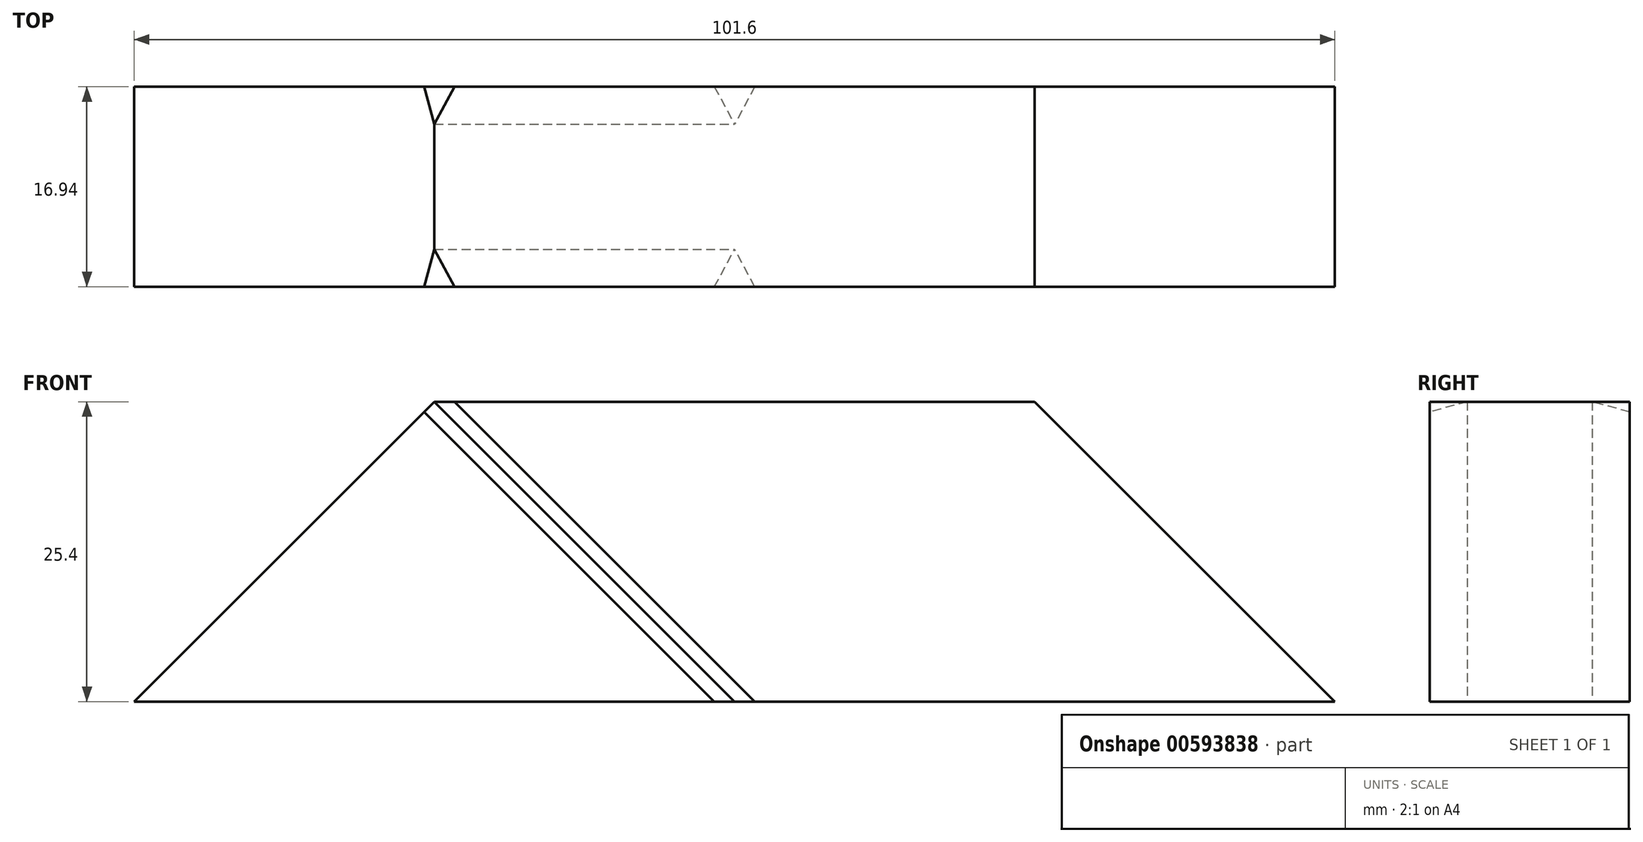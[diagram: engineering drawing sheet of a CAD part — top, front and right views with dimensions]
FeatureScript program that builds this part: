
annotation { "Feature Type Name" : "Feature", "Feature Type Description" : "" }
export const myFeature = defineFeature(function(context is Context, id is Id, definition is map)
    precondition{}
    {
        {
            var Q0;
            Q0=qCreatedBy(makeId("Front.planeOp"),FACE);
            var sketch = newSketch(context, id + "F0", { "sketchPlane" : qUnion([Q0])});
            skLineSegment(sketch, "E0.bottom", {"start": v(-50.8, 12.7) * mm, "end": v(50.8, 12.7) * mm});
            skLineSegment(sketch, "E0.top", {"start": v(-50.8, -12.7) * mm, "end": v(50.8, -12.7) * mm});
            skLineSegment(sketch, "E0.left", {"start": v(-50.8, 12.7) * mm, "end": v(-50.8, -12.7) * mm});
            skLineSegment(sketch, "E0.right", {"start": v(50.8, 12.7) * mm, "end": v(50.8, -12.7) * mm});
            skPoint(sketch, "E0.middle", {"position": v(0, 0) * mm});
            skSolve(sketch);
        }
        {
            var Q0;
            Q0=makeQuery(id+"F0.imprint","IMPRINT",FACE,{"disambiguationData":[TD([[makeQuery(id+"F0.imprint","IMPRINT",EDGE,{"derivedFrom":sQuery(id+"F0.wireOp",EDGE,"E0.bottom")}),-1.0]])]});
            extrude(context, id + "F1", {"entities" : qUnion([Q0]), "endBound" : BoundingType.SYMMETRIC, "depth" : 16.93 * mm, "offsetDistance" : 25.4 * mm});
        }
        {
            var Q0;
            Q0=makeQuery(id+"F1.opExtrude","SWEPT_EDGE",EDGE,{"disambiguationData":[OSD([sQuery(id+"F0.wireOp",EDGE,"E0.bottom"),sQuery(id+"F0.wireOp",EDGE,"E0.left")])]});
            var Q1;
            Q1=makeQuery(id+"F1.opExtrude","SWEPT_EDGE",EDGE,{"disambiguationData":[OSD([sQuery(id+"F0.wireOp",EDGE,"E0.bottom"),sQuery(id+"F0.wireOp",EDGE,"E0.right")])]});
            chamfer(context, id + "F2", {"entities" : qUnion([Q0, Q1]), "width" : 25.4 * mm, "tangentPropagation" : true});
        }
        {
            var Q0;
            Q0=makeQuery(id+"F1.opExtrude","SWEPT_FACE",FACE,{"disambiguationData":[OSD([sQuery(id+"F0.wireOp",EDGE,"E0.bottom")])]});
            var sketch = newSketch(context, id + "F3", { "sketchPlane" : qUnion([Q0])});
            skSolve(sketch);
        }
        {
            var Q0;
            {var subQ0=sQuery(id+"F0.wireOp",EDGE,"E0.bottom");Q0=makeQuery(id+"F3.imprint","IMPRINT",FACE,{"disambiguationData":[TD([[makeQuery(id+"F3.imprint","IMPRINT",EDGE,{"derivedFrom":makeQuery(id+"F1.opExtrude","CAP_EDGE",EDGE,{"disambiguationData":[OSD([subQ0])],"isStart":true})}),-1.0]])]});}
            var sketch = newSketch(context, id + "F4", { "sketchPlane" : qUnion([Q0])});
            skLineSegment(sketch, "E1", {"start": v(-25.4, -8.47) * mm, "end": v(-23.69, -8.47) * mm});
            skLineSegment(sketch, "E2", {"start": v(-23.69, -8.47) * mm, "end": v(-25.4, -5.3) * mm});
            skLineSegment(sketch, "E3.MirrorCS", {"start": v(-27.11, -8.47) * mm, "end": v(-25.4, -5.3) * mm});
            skLineSegment(sketch, "E4", {"start": v(-27.11, -8.47) * mm, "end": v(-23.69, -8.47) * mm});
            skLineSegment(sketch, "E5.MirrorCS", {"start": v(-25.4, 8.47) * mm, "end": v(-23.69, 8.47) * mm});
            skLineSegment(sketch, "E6.MirrorCS", {"start": v(-27.11, 8.47) * mm, "end": v(-23.69, 8.47) * mm});
            skLineSegment(sketch, "E7.MirrorCS", {"start": v(-27.11, 8.47) * mm, "end": v(-25.4, 5.3) * mm});
            skLineSegment(sketch, "E8.MirrorCS", {"start": v(-23.69, 8.47) * mm, "end": v(-25.4, 5.3) * mm});
            skSolve(sketch);
        }
        {
            var Q0;
            Q0=makeQuery(id+"F1.opExtrude","CAP_FACE",FACE,{"disambiguationData":[OSD([sQuery(id+"F0.wireOp",EDGE,"E0.bottom"),sQuery(id+"F0.wireOp",EDGE,"E0.top"),sQuery(id+"F0.wireOp",EDGE,"E0.left"),sQuery(id+"F0.wireOp",EDGE,"E0.right")])],"isStart":false});
            var sketch = newSketch(context, id + "F5", { "sketchPlane" : qUnion([Q0])});
            skLineSegment(sketch, "E9", {"start": v(-25.4, 12.7) * mm, "end": v(-25.4, -12.7) * mm, "construction": true});
            skLineSegment(sketch, "E10", {"start": v(-25.4, -12.7) * mm, "end": v(-50.8, -12.7) * mm, "construction": true});
            skLineSegment(sketch, "E11", {"start": v(-25.4, -12.7) * mm, "end": v(0, -12.7) * mm, "construction": true});
            skLineSegment(sketch, "E12", {"start": v(0, -12.7) * mm, "end": v(-25.4, 12.7) * mm});
            skSolve(sketch);
        }
        {
            var Q0;
            {var subQ0=sQuery(id+"F5.wireOp",EDGE,"E12");Q0=makeQuery(id+"F5.imprint","IMPRINT",FACE,{"disambiguationData":[TD([[makeQuery(id+"F5.imprint","IMPRINT",EDGE,{"derivedFrom":subQ0}),-1.0]])]});}
            var sketch = newSketch(context, id + "F6", { "sketchPlane" : qUnion([Q0])});
            skLineSegment(sketch, "E13.0.0", {"start": v(-25.4, 12.7) * mm, "end": v(0, -12.7) * mm, "construction": true});
            skLineSegment(sketch, "E13.0.1", {"start": v(0, -12.7) * mm, "end": v(50.8, -12.7) * mm, "construction": true});
            skLineSegment(sketch, "E13.0.2", {"start": v(50.8, -12.7) * mm, "end": v(25.4, 12.7) * mm, "construction": true});
            skLineSegment(sketch, "E13.0.3", {"start": v(25.4, 12.7) * mm, "end": v(-25.4, 12.7) * mm, "construction": true});
            skLineSegment(sketch, "E13.1.0", {"start": v(-50.8, -12.7) * mm, "end": v(0, -12.7) * mm});
            skLineSegment(sketch, "E13.1.1", {"start": v(0, -12.7) * mm, "end": v(-25.4, 12.7) * mm});
            skLineSegment(sketch, "E13.1.2", {"start": v(-25.4, 12.7) * mm, "end": v(-50.8, -12.7) * mm, "construction": true});
            skLineSegment(sketch, "E14", {"start": v(50.8, -12.7) * mm, "end": v(25.4, -12.7) * mm, "construction": true});
            skLineSegment(sketch, "E15", {"start": v(25.4, -12.7) * mm, "end": v(0, -12.7) * mm, "construction": true});
            skLineSegment(sketch, "E16", {"start": v(0, -12.7) * mm, "end": v(25.4, 12.7) * mm});
            skSolve(sketch);
        }
        {
            var Q0;
            {var subQ0=sQuery(id+"F4.wireOp",EDGE,"E3.MirrorCS");Q0=makeQuery(id+"F4.imprint","IMPRINT",FACE,{"disambiguationData":[TD([[makeQuery(id+"F4.imprint","IMPRINT",EDGE,{"derivedFrom":subQ0}),-1.0]])]});}
            var Q1;
            {var subQ4=sQuery(id+"F4.wireOp",EDGE,"E7.MirrorCS");Q1=makeQuery(id+"F4.imprint","IMPRINT",FACE,{"disambiguationData":[TD([[makeQuery(id+"F4.imprint","IMPRINT",EDGE,{"derivedFrom":subQ4}),1.0]])]});}
            var Q2;
            {var subQ0=sQuery(id+"F4.wireOp",EDGE,"E2");Q2=makeQuery(id+"F4.imprint","IMPRINT",FACE,{"disambiguationData":[TD([[makeQuery(id+"F4.imprint","IMPRINT",EDGE,{"derivedFrom":subQ0}),1.0]])]});}
            var Q3;
            {var subQ4=sQuery(id+"F4.wireOp",EDGE,"E8.MirrorCS");Q3=makeQuery(id+"F4.imprint","IMPRINT",FACE,{"disambiguationData":[TD([[makeQuery(id+"F4.imprint","IMPRINT",EDGE,{"derivedFrom":subQ4}),-1.0]])]});}
            var Q4;
            {var subQ4=sQuery(id+"F4.wireOp",EDGE,"dd271e9e-a8f9-4583-93ba-da34ee3789db0.MirrorCS");Q4=makeQuery(id+"F4.imprint","IMPRINT",FACE,{"disambiguationData":[TD([[makeQuery(id+"F4.imprint","IMPRINT",EDGE,{"derivedFrom":subQ4}),-1.0]])]});}
            var Q5;
            {var subQ4=sQuery(id+"F4.wireOp",EDGE,"3a3def27-543b-4b22-b4b6-f03de71b3d630.MirrorCS");Q5=makeQuery(id+"F4.imprint","IMPRINT",FACE,{"disambiguationData":[TD([[makeQuery(id+"F4.imprint","IMPRINT",EDGE,{"derivedFrom":subQ4}),1.0]])]});}
            var Q6;
            {var subQ0=sQuery(id+"F4.wireOp",EDGE,"d168a0cd-3c3a-453f-922a-891af3fde8110.MirrorCS");Q6=makeQuery(id+"F4.imprint","IMPRINT",FACE,{"disambiguationData":[TD([[makeQuery(id+"F4.imprint","IMPRINT",EDGE,{"derivedFrom":subQ0}),-1.0]])]});}
            var Q7;
            {var subQ0=sQuery(id+"F4.wireOp",EDGE,"236fdeae-9e82-49a9-9917-dcd104433e210.MirrorCS");Q7=makeQuery(id+"F4.imprint","IMPRINT",FACE,{"disambiguationData":[TD([[makeQuery(id+"F4.imprint","IMPRINT",EDGE,{"derivedFrom":subQ0}),1.0]])]});}
            var Q8;
            Q8 = qConstructionFilter(qBodyType(qCreatedBy(id + "F5" ,EDGE), BodyType.WIRE), ConstructionObject.NO);
            sweep(context, id + "F7", {"operationType" : NewBodyOperationType.REMOVE, "profiles" : qUnion([Q0, Q1, Q2, Q3, Q4, Q5, Q6, Q7]), "path" : qUnion([Q8])});
        }
    });
